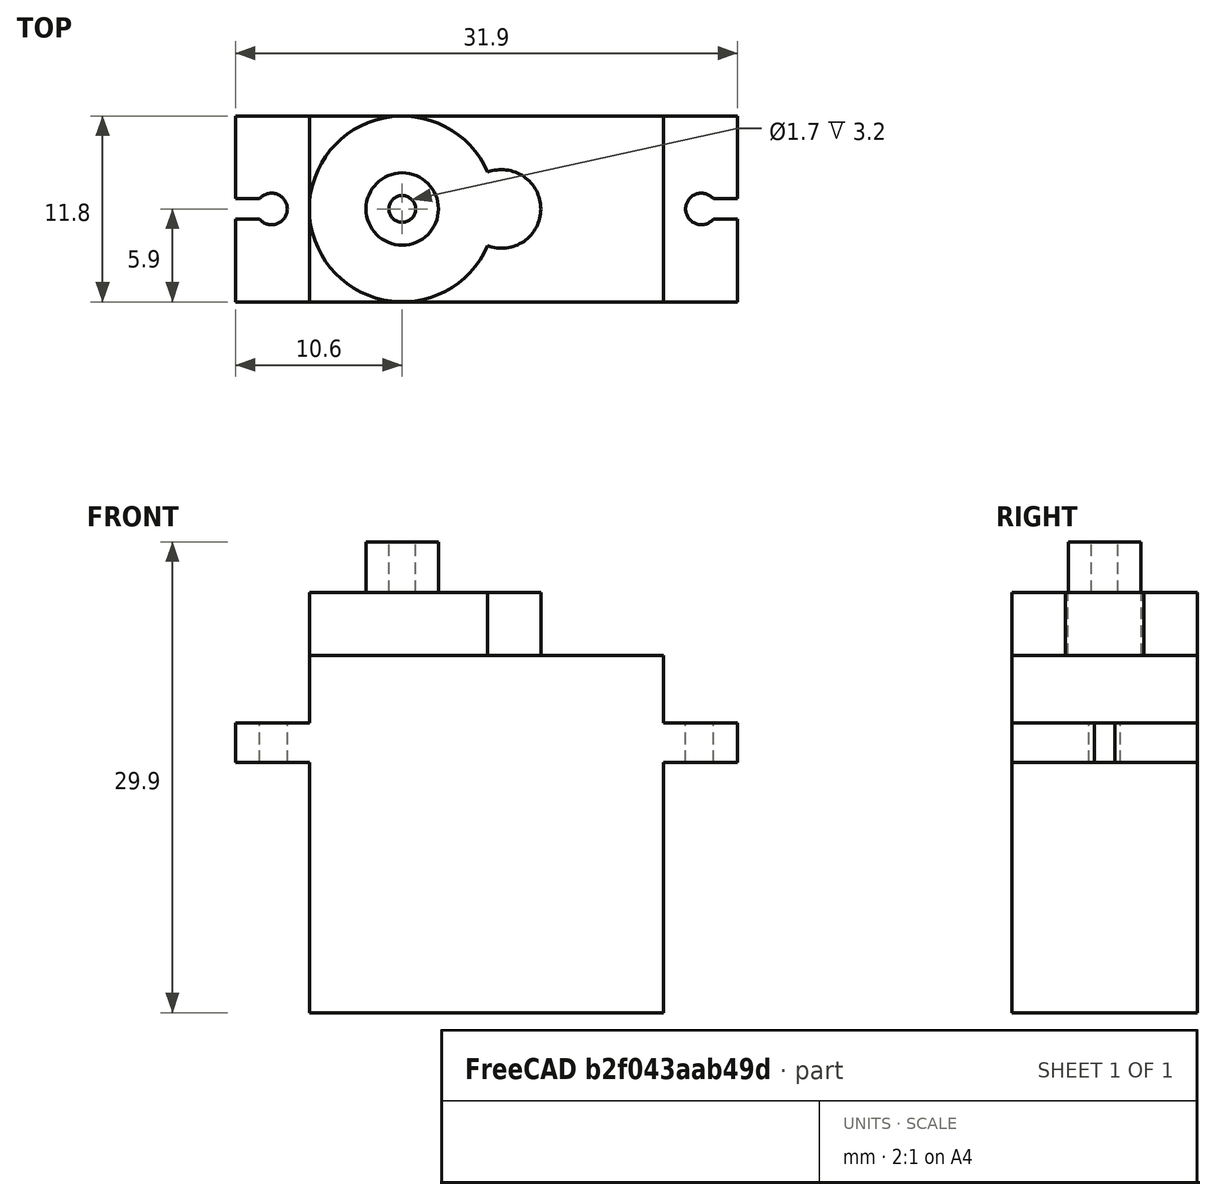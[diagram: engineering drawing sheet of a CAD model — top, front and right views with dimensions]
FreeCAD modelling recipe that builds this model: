
FCSTD DOCUMENT  (FreeCAD 0.19R24291 (Git))
Label: servo
License: All rights reserved
LicenseURL: http://en.wikipedia.org/wiki/All_rights_reserved
objects: Part::Cylinder×6, Part::MultiFuse×6, Part::Box×4, Part::Cut×3
note: 19 computed .brp shape members not serialized (recipe doc carries the construction recipe); baked Part::Feature solids carry a one-line shape summary decoded from their .brp

FEATURE [Part::Box] Box  label="aleta"
  AttacherType = Attacher::AttachEngine3D
  Height = 2.5
  Length = 31.9
  Width = 11.8
FEATURE [Part::Cylinder] Cylinder  label="taladro-cilindro"
  Angle = 360
  AttacherType = Attacher::AttachEngine3D
  Height = 5
  Radius = 1
FEATURE [Part::Box] Box001  label="taladro-cubo"
  AttacherType = Attacher::AttachEngine3D
  Height = 5
  Length = 4.3
  Placement = pos=(0,-0.65,0) rot=(0,0,1;0rad)
  Width = 1.3
FEATURE [Part::MultiFuse] Fusion  label="taladro 1"
  Placement = pos=(29.6,5.9,-1) rot=(0,0,1;0rad)
  Refine = true
  Shapes = -> [Cylinder,Box001]
FEATURE [Part::Box] Box002  label="taladro-cubo001"
  AttacherType = Attacher::AttachEngine3D
  Height = 5
  Length = 4.3
  Placement = pos=(0,-0.65,0) rot=(0,0,1;0rad)
  Width = 1.3
FEATURE [Part::Cylinder] Cylinder001  label="taladro-cilindro001"
  Angle = 360
  AttacherType = Attacher::AttachEngine3D
  Height = 5
  Radius = 1
FEATURE [Part::MultiFuse] Fusion001  label="taladro 2"
  Placement = pos=(2.3,5.9,-1) rot=(0,0,1;3.14159rad)
  Refine = true
  Shapes = -> [Cylinder001,Box002]
FEATURE [Part::Cut] Cut
  Base = -> Box
  Refine = true
  Tool = -> Fusion
FEATURE [Part::Cut] Cut001  label="aleta-con-taladros"
  Base = -> Cut
  Placement = pos=(-4.7,0,15.9) rot=(0,0,1;0rad)
  Refine = true
  Tool = -> Fusion001
FEATURE [Part::Box] Box003  label="base"
  AttacherType = Attacher::AttachEngine3D
  Height = 22.7
  Length = 22.5
  Width = 11.8
FEATURE [Part::Cylinder] Cylinder002  label="Cylinder"
  Angle = 360
  AttacherType = Attacher::AttachEngine3D
  Height = 4
  Radius = 5.9
FEATURE [Part::Cylinder] Cylinder003
  Angle = 360
  AttacherType = Attacher::AttachEngine3D
  Height = 4
  Placement = pos=(6.3,0,0) rot=(0,0,1;0rad)
  Radius = 2.5
FEATURE [Part::MultiFuse] Fusion002  label="soporte-rotor"
  Placement = pos=(5.9,5.9,22.7) rot=(0,0,1;0rad)
  Refine = true
  Shapes = -> [Cylinder002,Cylinder003]
FEATURE [Part::Cylinder] Cylinder004
  Angle = 360
  AttacherType = Attacher::AttachEngine3D
  Height = 3.3
  Placement = pos=(0,0,-0.1) rot=(0,0,1;0rad)
  Radius = 2.3
FEATURE [Part::Cylinder] Cylinder005
  Angle = 360
  AttacherType = Attacher::AttachEngine3D
  Height = 4
  Placement = pos=(0,0,-0.5) rot=(0,0,1;0rad)
  Radius = 0.85
FEATURE [Part::Cut] Cut002  label="rotor"
  Base = -> Cylinder004
  Placement = pos=(5.9,5.9,26.7) rot=(0,0,1;0rad)
  Refine = true
  Tool = -> Cylinder005
FEATURE [Part::MultiFuse] Fusion003  label="base-con-aleta"
  Refine = true
  Shapes = -> [Cut001,Box003]
FEATURE [Part::MultiFuse] Fusion004  label="soporte-con-rotor"
  Refine = true
  Shapes = -> [Fusion002,Cut002]
FEATURE [Part::MultiFuse] Fusion005  label="micro-servo-SG-90"
  Refine = true
  Shapes = -> [Fusion003,Fusion004]
